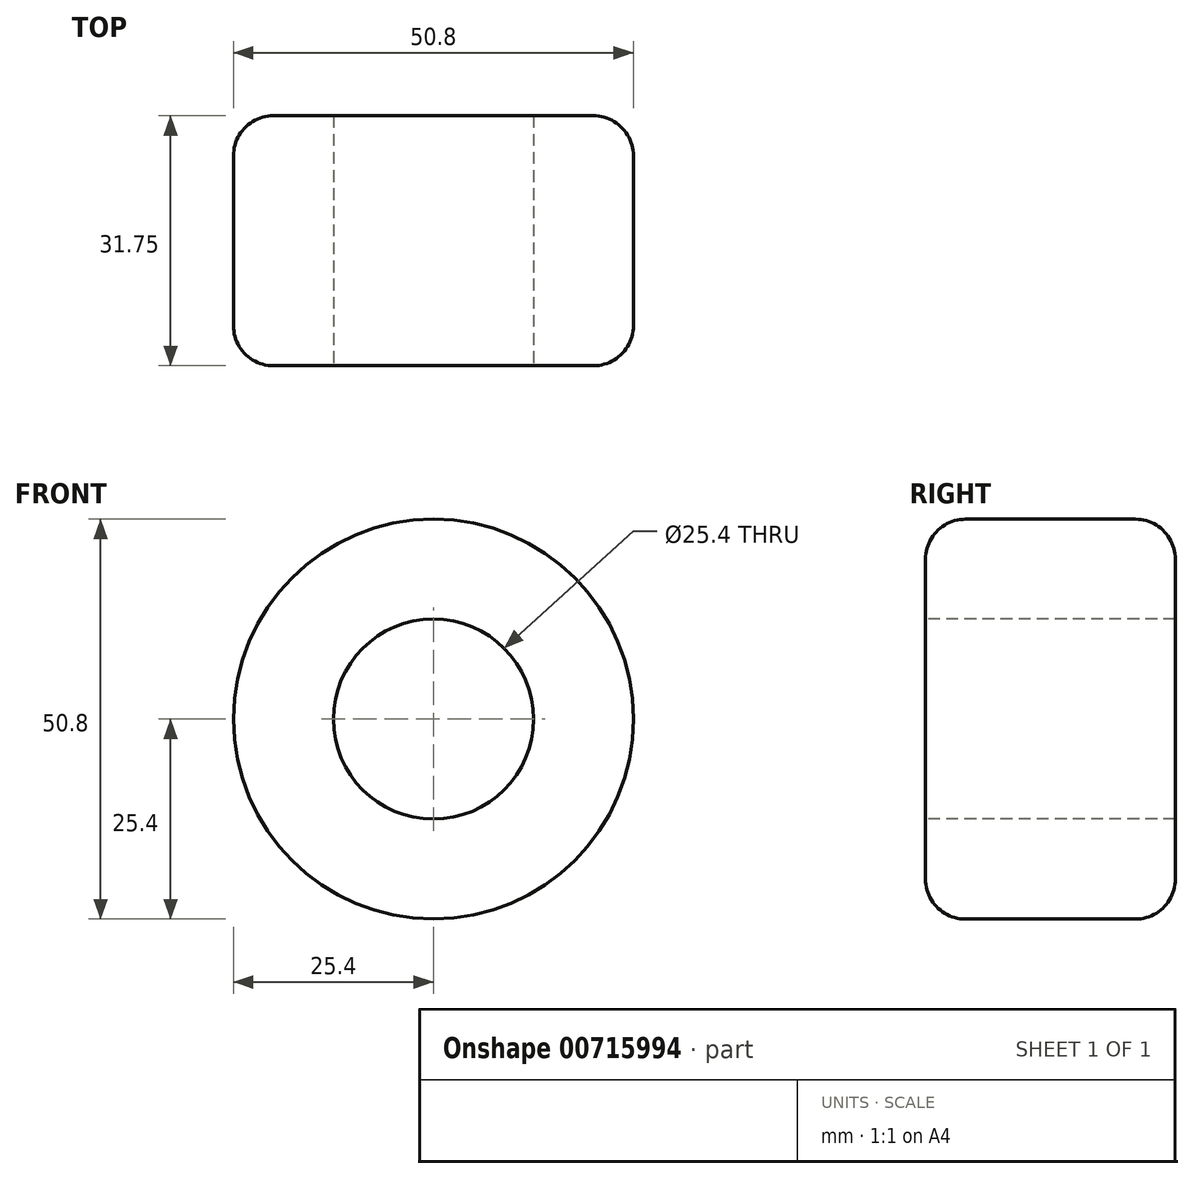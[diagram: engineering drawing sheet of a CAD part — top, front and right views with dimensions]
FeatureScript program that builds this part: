
annotation { "Feature Type Name" : "Feature", "Feature Type Description" : "" }
export const myFeature = defineFeature(function(context is Context, id is Id, definition is map)
    precondition{}
    {
        {
            var Q0;
            Q0=qCreatedBy(makeId("Front.planeOp"),FACE);
            var sketch = newSketch(context, id + "F0", { "sketchPlane" : qUnion([Q0])});
            skCircle(sketch, "E0", {"center": v(0, 0) * mm, "radius": 12.7 * mm});
            skCircle(sketch, "E1", {"center": v(0, 0) * mm, "radius": 25.4 * mm});
            skSolve(sketch);
        }
        {
            var Q0;
            Q0=makeQuery(id+"F0.imprint","IMPRINT",FACE,{"disambiguationData":[TD([[makeQuery(id+"F0.imprint","IMPRINT",EDGE,{"derivedFrom":sQuery(id+"F0.wireOp",EDGE,"E0")}),-1.0]])]});
            extrude(context, id + "F1", {"entities" : qUnion([Q0]), "oppositeDirection" : true, "depth" : 31.75 * mm, "offsetDistance" : 25.4 * mm});
        }
        {
            var Q0;
            Q0=makeQuery(id+"F1.opExtrude","CAP_EDGE",EDGE,{"disambiguationData":[OSD([sQuery(id+"F0.wireOp",EDGE,"E1")])],"isStart":true});
            var Q1;
            Q1=makeQuery(id+"F1.opExtrude","CAP_EDGE",EDGE,{"disambiguationData":[OSD([sQuery(id+"F0.wireOp",EDGE,"E1")])],"isStart":false});
            fillet(context, id + "F2", {"entities" : qUnion([Q0, Q1]), "radius" : 5.08 * mm, "tangentPropagation" : true, "allowEdgeOverflow" : false});
        }
    });
